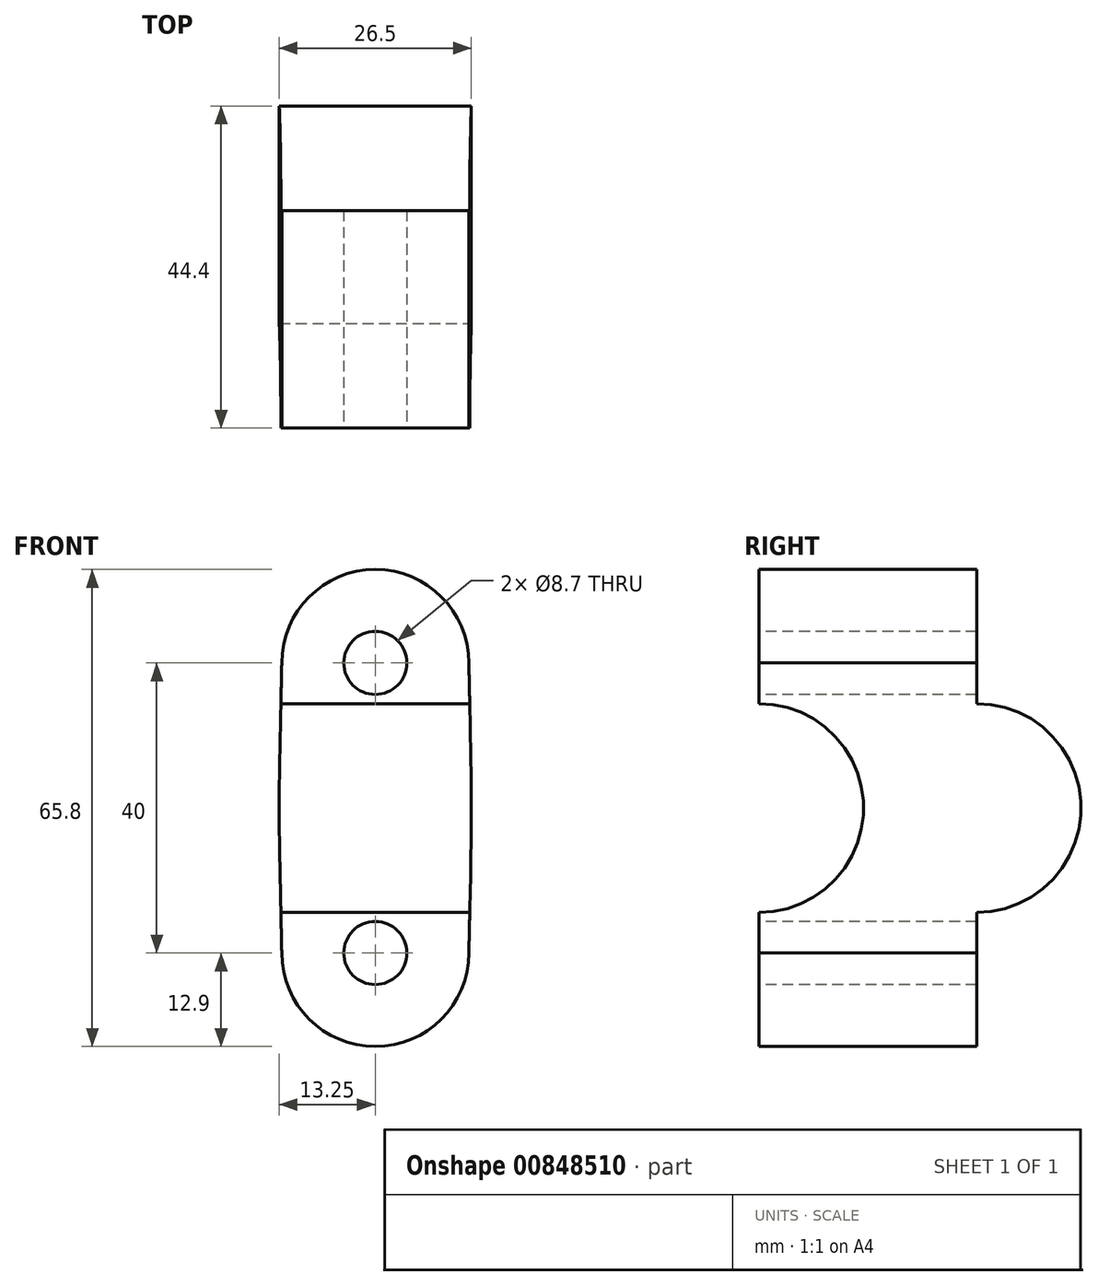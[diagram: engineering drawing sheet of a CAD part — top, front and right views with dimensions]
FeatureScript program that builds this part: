
annotation { "Feature Type Name" : "Feature", "Feature Type Description" : "" }
export const myFeature = defineFeature(function(context is Context, id is Id, definition is map)
    precondition{}
    {
        {
            var Q0;
            Q0=qCreatedBy(makeId("Front.planeOp"),FACE);
            var sketch = newSketch(context, id + "F0", { "sketchPlane" : qUnion([Q0])});
            skArc(sketch, "E0", {"start": v(12.9, 20) * mm, "mid": v(0, 32.9) * mm, "end": v(-12.9, 20) * mm});
            skArc(sketch, "E1", {"start": v(-12.9, -20) * mm, "mid": v(0, -32.9) * mm, "end": v(12.9, -20) * mm});
            skLineSegment(sketch, "E2", {"start": v(-12.9, 20) * mm, "end": v(12.9, 20) * mm, "construction": true});
            skLineSegment(sketch, "E3", {"start": v(-12.9, -20) * mm, "end": v(12.9, -20) * mm, "construction": true});
            skPoint(sketch, "E4", {"position": v(-13.25, 0) * mm});
            skPoint(sketch, "E5.MirrorP", {"position": v(13.25, 0) * mm});
            skFitSpline(sketch, "E6", {"points": [v(-12.9, 20) * mm, v(-13.25, 0) * mm, v(-12.9, -20) * mm], "startDerivative": vector(-1.05, -50.3) * mm, "endDerivative": vector(1.05, -50.3) * mm});
            skFitSpline(sketch, "E7", {"points": [v(12.9, 20) * mm, v(13.25, 0) * mm, v(12.9, -20) * mm], "startDerivative": vector(1.05, -50.3) * mm, "endDerivative": vector(-1.05, -50.3) * mm});
            skCircle(sketch, "E8", {"center": v(0, 20) * mm, "radius": 4.35 * mm});
            skCircle(sketch, "E9.MirrorC", {"center": v(0, -20) * mm, "radius": 4.35 * mm});
            skSolve(sketch);
        }
        {
            var Q0;
            Q0=makeQuery(id+"F0.imprint","IMPRINT",FACE,{"disambiguationData":[TD([[makeQuery(id+"F0.imprint","IMPRINT",EDGE,{"derivedFrom":sQuery(id+"F0.wireOp",EDGE,"E0")}),1.0]])]});
            extrude(context, id + "F1", {"entities" : qUnion([Q0]), "oppositeDirection" : true, "depth" : 50 * mm, "offsetDistance" : 25 * mm});
        }
        {
            var Q0;
            Q0=qCreatedBy(makeId("Right.planeOp"),FACE);
            var sketch = newSketch(context, id + "F2", { "sketchPlane" : qUnion([Q0])});
            skFitSpline(sketch, "E10.0.0", {"points": [v(50, -25.15) * mm, v(50, -16.77) * mm, v(50, 0) * mm, v(50, 16.77) * mm, v(50, 25.15) * mm], "construction": true});
            skLineSegment(sketch, "E10.0.1", {"start": v(50, 20) * mm, "end": v(50, 32.9) * mm, "construction": true});
            skFitSpline(sketch, "E10.0.2", {"points": [v(50, 25.15) * mm, v(50, 16.77) * mm, v(50, 0) * mm, v(50, -16.77) * mm, v(50, -25.15) * mm], "construction": true});
            skLineSegment(sketch, "E10.0.3", {"start": v(50, -20) * mm, "end": v(50, -32.9) * mm, "construction": true});
            skFitSpline(sketch, "E11.0.0", {"points": [v(0, 25.15) * mm, v(0, 16.77) * mm, v(0, 0) * mm, v(0, -16.77) * mm, v(0, -25.15) * mm], "construction": true});
            skLineSegment(sketch, "E11.0.1", {"start": v(0, -20) * mm, "end": v(0, -32.9) * mm, "construction": true});
            skFitSpline(sketch, "E11.0.2", {"points": [v(0, -25.15) * mm, v(0, -16.77) * mm, v(0, 0) * mm, v(0, 16.77) * mm, v(0, 25.15) * mm], "construction": true});
            skLineSegment(sketch, "E11.0.3", {"start": v(0, 20) * mm, "end": v(0, 32.9) * mm, "construction": true});
            skArc(sketch, "E12", {"start": v(0, -14.4) * mm, "mid": v(14.4, 0) * mm, "end": v(0, 14.4) * mm});
            skLineSegment(sketch, "E13", {"start": v(50, 32.9) * mm, "end": v(30, 32.9) * mm});
            skLineSegment(sketch, "E14", {"start": v(30, 32.9) * mm, "end": v(30, 14.4) * mm});
            skLineSegment(sketch, "E15", {"start": v(50, 32.9) * mm, "end": v(50, -32.9) * mm});
            skLineSegment(sketch, "E16", {"start": v(30, -32.9) * mm, "end": v(30, -14.4) * mm});
            skArc(sketch, "E17", {"start": v(30, -14.4) * mm, "mid": v(44.4, 0) * mm, "end": v(30, 14.4) * mm});
            skLineSegment(sketch, "E18", {"start": v(0, 14.4) * mm, "end": v(0, -14.4) * mm});
            skLineSegment(sketch, "E19", {"start": v(50, -32.9) * mm, "end": v(30, -32.9) * mm});
            skSolve(sketch);
        }
        {
            var Q0;
            Q0 = qSketchRegion(id + "F2", true);
            extrude(context, id + "F3", {"entities" : qUnion([Q0]), "operationType" : NewBodyOperationType.REMOVE, "endBound" : BoundingType.SYMMETRIC, "oppositeDirection" : true, "depth" : 30 * mm, "offsetDistance" : 25 * mm});
        }
    });
